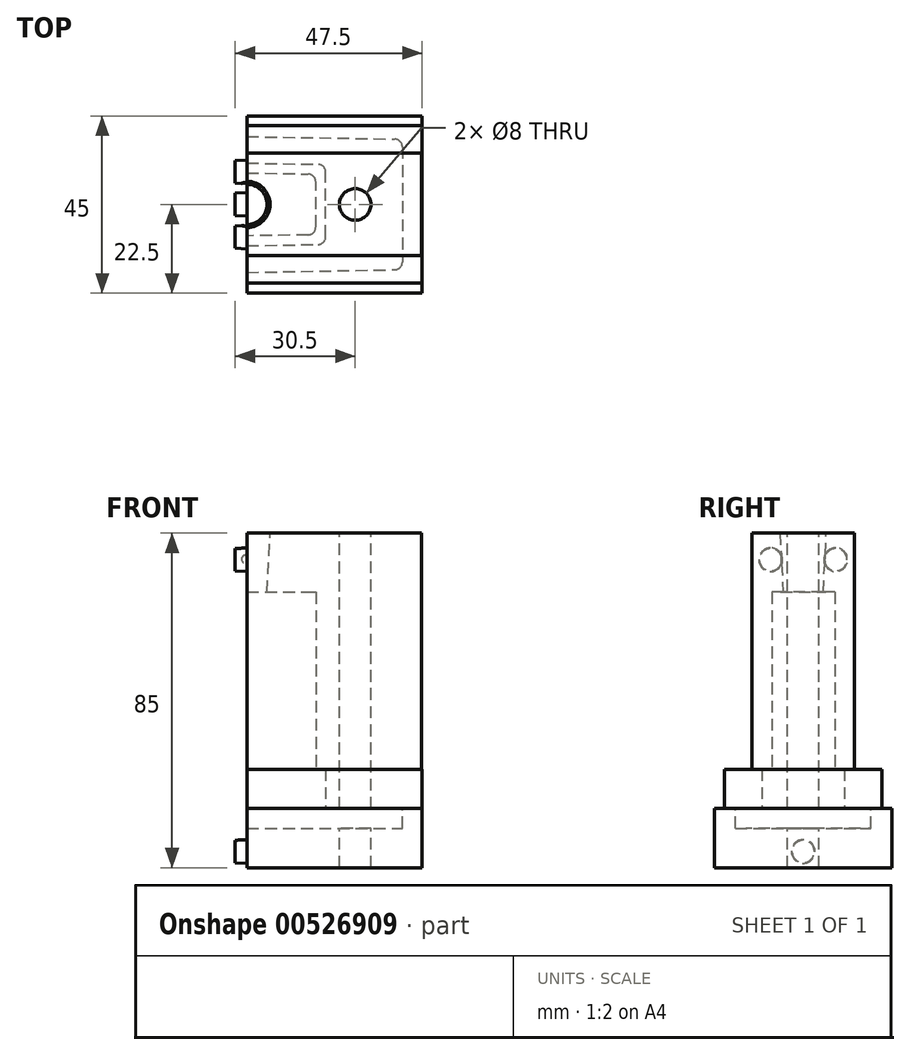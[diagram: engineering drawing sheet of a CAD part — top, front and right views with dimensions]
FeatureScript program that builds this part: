
annotation { "Feature Type Name" : "Feature", "Feature Type Description" : "" }
export const myFeature = defineFeature(function(context is Context, id is Id, definition is map)
    precondition{}
    {
        {
            var Q0;
            Q0=qCreatedBy(makeId("Top.planeOp"),FACE);
            var sketch = newSketch(context, id + "F0", { "sketchPlane" : qUnion([Q0])});
            skLineSegment(sketch, "E0.bottom", {"start": v(44.4, -13) * mm, "end": v(-44.4, -13) * mm});
            skLineSegment(sketch, "E0.top", {"start": v(44.4, 13) * mm, "end": v(-44.4, 13) * mm});
            skLineSegment(sketch, "E0.left", {"start": v(44.4, -13) * mm, "end": v(44.4, 13) * mm});
            skLineSegment(sketch, "E0.right", {"start": v(-44.4, -13) * mm, "end": v(-44.4, 13) * mm});
            skPoint(sketch, "E0.middle", {"position": v(0, 0) * mm});
            skSolve(sketch);
        }
        {
            var Q0;
            Q0 = qSketchRegion(id + "F0", true);
            extrude(context, id + "F1", {"entities" : qUnion([Q0]), "depth" : 60 * mm, "offsetDistance" : 25 * mm});
        }
        {
            var Q0;
            Q0=makeQuery(id+"F1.opExtrude","CAP_FACE",FACE,{"disambiguationData":[OSD([sQuery(id+"F0.wireOp",EDGE,"E0.bottom"),sQuery(id+"F0.wireOp",EDGE,"E0.top"),sQuery(id+"F0.wireOp",EDGE,"E0.left"),sQuery(id+"F0.wireOp",EDGE,"E0.right")])],"isStart":true});
            var sketch = newSketch(context, id + "F2", { "sketchPlane" : qUnion([Q0])});
            skPoint(sketch, "E1.middle", {"position": v(0, 0) * mm});
            skLineSegment(sketch, "E2", {"start": v(0, -8) * mm, "end": v(-17.5, -7.7) * mm});
            skLineSegment(sketch, "E3", {"start": v(0, -8) * mm, "end": v(17.5, -7.7) * mm});
            skLineSegment(sketch, "E4", {"start": v(0, 8) * mm, "end": v(-17.5, 7.7) * mm});
            skLineSegment(sketch, "E5", {"start": v(17.5, 7.7) * mm, "end": v(0, 8) * mm});
            skLineSegment(sketch, "E6", {"start": v(-17.5, 7.7) * mm, "end": v(-17.5, -7.7) * mm});
            skLineSegment(sketch, "E7", {"start": v(17.5, 7.7) * mm, "end": v(17.5, -7.7) * mm});
            skSolve(sketch);
        }
        {
            var Q0;
            Q0 = qSketchRegion(id + "F2", true);
            extrude(context, id + "F3", {"entities" : qUnion([Q0]), "operationType" : NewBodyOperationType.REMOVE, "oppositeDirection" : true, "depth" : 45 * mm, "offsetDistance" : 25 * mm});
        }
        {
            var Q0;
            Q0=makeQuery(id+"F3.boolean.opBoolean","COPY",EDGE,{"derivedFrom":makeQuery(id+"F3.opExtrude","SWEPT_EDGE",EDGE,{"disambiguationData":[OSD([sQuery(id+"F2.wireOp",EDGE,"E2"),sQuery(id+"F2.wireOp",EDGE,"E6")])]})});
            var Q1;
            Q1=makeQuery(id+"F3.boolean.opBoolean","COPY",EDGE,{"derivedFrom":makeQuery(id+"F3.opExtrude","SWEPT_EDGE",EDGE,{"disambiguationData":[OSD([sQuery(id+"F2.wireOp",EDGE,"E4"),sQuery(id+"F2.wireOp",EDGE,"E6")])]})});
            var Q2;
            Q2=makeQuery(id+"F3.boolean.opBoolean","COPY",EDGE,{"derivedFrom":makeQuery(id+"F3.opExtrude","SWEPT_EDGE",EDGE,{"disambiguationData":[OSD([sQuery(id+"F2.wireOp",EDGE,"E5"),sQuery(id+"F2.wireOp",EDGE,"E7")])]})});
            var Q3;
            Q3=makeQuery(id+"F3.boolean.opBoolean","COPY",EDGE,{"derivedFrom":makeQuery(id+"F3.opExtrude","SWEPT_EDGE",EDGE,{"disambiguationData":[OSD([sQuery(id+"F2.wireOp",EDGE,"E3"),sQuery(id+"F2.wireOp",EDGE,"E7")])]})});
            fillet(context, id + "F4", {"entities" : qUnion([Q0, Q1, Q2, Q3]), "radius" : 2 * mm, "tangentPropagation" : true, "allowEdgeOverflow" : false});
        }
        {
            var Q0;
            Q0=makeQuery(id+"F1.opExtrude","CAP_FACE",FACE,{"disambiguationData":[OSD([sQuery(id+"F0.wireOp",EDGE,"E0.bottom"),sQuery(id+"F0.wireOp",EDGE,"E0.top"),sQuery(id+"F0.wireOp",EDGE,"E0.left"),sQuery(id+"F0.wireOp",EDGE,"E0.right")])],"isStart":true});
            var sketch = newSketch(context, id + "F5", { "sketchPlane" : qUnion([Q0])});
            skLineSegment(sketch, "E8.bottom", {"start": v(44.45, -20) * mm, "end": v(-44.45, -20) * mm});
            skLineSegment(sketch, "E8.top", {"start": v(44.45, 20) * mm, "end": v(-44.45, 20) * mm});
            skLineSegment(sketch, "E8.left", {"start": v(44.45, -20) * mm, "end": v(44.45, 20) * mm});
            skLineSegment(sketch, "E8.right", {"start": v(-44.45, -20) * mm, "end": v(-44.45, 20) * mm});
            skPoint(sketch, "E8.middle", {"position": v(0, 0) * mm});
            skSolve(sketch);
        }
        {
            var Q0;
            Q0 = qSketchRegion(id + "F5", true);
            extrude(context, id + "F6", {"entities" : qUnion([Q0]), "operationType" : NewBodyOperationType.ADD, "depth" : 10 * mm, "offsetDistance" : 25 * mm});
        }
        {
            var Q0;
            Q0=makeQuery(id+"F6.opExtrude","CAP_FACE",FACE,{"disambiguationData":[OSD([sQuery(id+"F5.wireOp",EDGE,"E8.bottom"),sQuery(id+"F5.wireOp",EDGE,"E8.top"),sQuery(id+"F5.wireOp",EDGE,"E8.left"),sQuery(id+"F5.wireOp",EDGE,"E8.right")])],"isStart":false});
            var sketch = newSketch(context, id + "F7", { "sketchPlane" : qUnion([Q0])});
            skPoint(sketch, "E9.middle", {"position": v(0, 0) * mm});
            skLineSegment(sketch, "E10", {"start": v(0, -10.5) * mm, "end": v(20, -10.15) * mm});
            skLineSegment(sketch, "E11", {"start": v(0, -10.5) * mm, "end": v(-20, -10.15) * mm});
            skLineSegment(sketch, "E12", {"start": v(-20, 10.15) * mm, "end": v(0, 10.5) * mm});
            skLineSegment(sketch, "E13", {"start": v(0, 10.5) * mm, "end": v(20, 10.15) * mm});
            skLineSegment(sketch, "E14", {"start": v(20, 10.15) * mm, "end": v(20, -10.15) * mm});
            skLineSegment(sketch, "E15", {"start": v(-20, 10.15) * mm, "end": v(-20, -10.15) * mm});
            skSolve(sketch);
        }
        {
            var Q0;
            Q0 = qSketchRegion(id + "F7", true);
            extrude(context, id + "F8", {"entities" : qUnion([Q0]), "operationType" : NewBodyOperationType.REMOVE, "oppositeDirection" : true, "depth" : 10 * mm, "offsetDistance" : 25 * mm});
        }
        {
            var Q0;
            Q0=makeQuery(id+"F8.boolean.opBoolean","COPY",EDGE,{"derivedFrom":makeQuery(id+"F8.opExtrude","SWEPT_EDGE",EDGE,{"disambiguationData":[OSD([sQuery(id+"F7.wireOp",EDGE,"E11"),sQuery(id+"F7.wireOp",EDGE,"E15")])]})});
            var Q1;
            Q1=makeQuery(id+"F8.boolean.opBoolean","COPY",EDGE,{"derivedFrom":makeQuery(id+"F8.opExtrude","SWEPT_EDGE",EDGE,{"disambiguationData":[OSD([sQuery(id+"F7.wireOp",EDGE,"E12"),sQuery(id+"F7.wireOp",EDGE,"E15")])]})});
            var Q2;
            Q2=makeQuery(id+"F8.boolean.opBoolean","COPY",EDGE,{"derivedFrom":makeQuery(id+"F8.opExtrude","SWEPT_EDGE",EDGE,{"disambiguationData":[OSD([sQuery(id+"F7.wireOp",EDGE,"E10"),sQuery(id+"F7.wireOp",EDGE,"E14")])]})});
            var Q3;
            Q3=makeQuery(id+"F8.boolean.opBoolean","COPY",EDGE,{"derivedFrom":makeQuery(id+"F8.opExtrude","SWEPT_EDGE",EDGE,{"disambiguationData":[OSD([sQuery(id+"F7.wireOp",EDGE,"E13"),sQuery(id+"F7.wireOp",EDGE,"E14")])]})});
            fillet(context, id + "F9", {"entities" : qUnion([Q0, Q1, Q2, Q3]), "radius" : 2 * mm, "tangentPropagation" : true, "allowEdgeOverflow" : false});
        }
        {
            var Q0;
            Q0=makeQuery(id+"F6.opExtrude","CAP_FACE",FACE,{"disambiguationData":[OSD([sQuery(id+"F5.wireOp",EDGE,"E8.bottom"),sQuery(id+"F5.wireOp",EDGE,"E8.top"),sQuery(id+"F5.wireOp",EDGE,"E8.left"),sQuery(id+"F5.wireOp",EDGE,"E8.right")])],"isStart":false});
            var sketch = newSketch(context, id + "F10", { "sketchPlane" : qUnion([Q0])});
            skLineSegment(sketch, "E16.bottom", {"start": v(44.5, -22.5) * mm, "end": v(-44.5, -22.5) * mm});
            skLineSegment(sketch, "E16.top", {"start": v(44.5, 22.5) * mm, "end": v(-44.5, 22.5) * mm});
            skLineSegment(sketch, "E16.left", {"start": v(44.5, -22.5) * mm, "end": v(44.5, 22.5) * mm});
            skLineSegment(sketch, "E16.right", {"start": v(-44.5, -22.5) * mm, "end": v(-44.5, 22.5) * mm});
            skPoint(sketch, "E16.middle", {"position": v(0, 0) * mm});
            skSolve(sketch);
        }
        {
            var Q0;
            Q0 = qSketchRegion(id + "F10", true);
            extrude(context, id + "F11", {"entities" : qUnion([Q0]), "operationType" : NewBodyOperationType.ADD, "depth" : 15 * mm, "offsetDistance" : 25 * mm});
        }
        {
            var Q0;
            {var subQ0=sQuery(id+"F10.wireOp",EDGE,"E16.bottom");var subQ1=sQuery(id+"F10.wireOp",EDGE,"E16.top");var subQ2=sQuery(id+"F10.wireOp",EDGE,"E16.left");var subQ3=sQuery(id+"F10.wireOp",EDGE,"E16.right");Q0=makeQuery(id+"F11.boolean.opBoolean","SPLIT",FACE,{"disambiguationData":[TD([makeQuery(id+"F6.opExtrude","SWEPT_FACE",FACE,{"disambiguationData":[OSD([sQuery(id+"F5.wireOp",EDGE,"E8.bottom")])]})])],"derivedFrom":makeQuery(id+"F11.opExtrude","CAP_FACE",FACE,{"disambiguationData":[OSD([subQ0,subQ1,subQ2,subQ3])],"isStart":true})});}
            var sketch = newSketch(context, id + "F12", { "sketchPlane" : qUnion([Q0])});
            skPoint(sketch, "E17.middle", {"position": v(0, 0) * mm});
            skLineSegment(sketch, "E18", {"start": v(0, -17.25) * mm, "end": v(39.5, -16.56) * mm});
            skLineSegment(sketch, "E19", {"start": v(0, -17.25) * mm, "end": v(-44.45, -17.25) * mm});
            skLineSegment(sketch, "E20", {"start": v(-39.5, -16.56) * mm, "end": v(0, -17.25) * mm});
            skLineSegment(sketch, "E21", {"start": v(0, 17.25) * mm, "end": v(-39.5, 16.56) * mm});
            skLineSegment(sketch, "E22", {"start": v(0, 17.25) * mm, "end": v(39.5, 16.56) * mm});
            skLineSegment(sketch, "E23", {"start": v(-39.5, 16.56) * mm, "end": v(-39.5, -16.56) * mm});
            skLineSegment(sketch, "E24", {"start": v(39.5, 16.56) * mm, "end": v(39.5, -16.56) * mm});
            skSolve(sketch);
        }
        {
            var Q0;
            Q0 = qSketchRegion(id + "F12", true);
            extrude(context, id + "F13", {"entities" : qUnion([Q0]), "operationType" : NewBodyOperationType.REMOVE, "oppositeDirection" : true, "depth" : 5 * mm, "offsetDistance" : 25 * mm});
        }
        {
            var Q0;
            Q0=makeQuery(id+"F13.boolean.opBoolean","COPY",EDGE,{"derivedFrom":makeQuery(id+"F13.opExtrude","SWEPT_EDGE",EDGE,{"disambiguationData":[OSD([sQuery(id+"F12.wireOp",EDGE,"E21"),sQuery(id+"F12.wireOp",EDGE,"E23")])]})});
            var Q1;
            Q1=makeQuery(id+"F13.boolean.opBoolean","COPY",EDGE,{"derivedFrom":makeQuery(id+"F13.opExtrude","SWEPT_EDGE",EDGE,{"disambiguationData":[OSD([sQuery(id+"F12.wireOp",EDGE,"E20"),sQuery(id+"F12.wireOp",EDGE,"E23")])]})});
            var Q2;
            Q2=makeQuery(id+"F13.boolean.opBoolean","COPY",EDGE,{"derivedFrom":makeQuery(id+"F13.opExtrude","SWEPT_EDGE",EDGE,{"disambiguationData":[OSD([sQuery(id+"F12.wireOp",EDGE,"E18"),sQuery(id+"F12.wireOp",EDGE,"E24")])]})});
            var Q3;
            Q3=makeQuery(id+"F13.boolean.opBoolean","COPY",EDGE,{"derivedFrom":makeQuery(id+"F13.opExtrude","SWEPT_EDGE",EDGE,{"disambiguationData":[OSD([sQuery(id+"F12.wireOp",EDGE,"E22"),sQuery(id+"F12.wireOp",EDGE,"E24")])]})});
            fillet(context, id + "F14", {"entities" : qUnion([Q0, Q1, Q2, Q3]), "radius" : 2 * mm, "tangentPropagation" : true, "allowEdgeOverflow" : false});
        }
        {
            var Q0;
            Q0=makeQuery(id+"F1.opExtrude","CAP_FACE",FACE,{"disambiguationData":[OSD([sQuery(id+"F0.wireOp",EDGE,"E0.bottom"),sQuery(id+"F0.wireOp",EDGE,"E0.top"),sQuery(id+"F0.wireOp",EDGE,"E0.left"),sQuery(id+"F0.wireOp",EDGE,"E0.right")])],"isStart":false});
            var sketch = newSketch(context, id + "F15", { "sketchPlane" : qUnion([Q0])});
            skCircle(sketch, "E25", {"center": v(27.5, 0) * mm, "radius": 4 * mm});
            skCircle(sketch, "E26", {"center": v(-27.5, 0) * mm, "radius": 4.67 * mm});
            skSolve(sketch);
        }
        {
            var Q0;
            Q0=makeQuery(id+"F15.imprint","IMPRINT",FACE,{"disambiguationData":[TD([[makeQuery(id+"F15.imprint","IMPRINT",EDGE,{"derivedFrom":sQuery(id+"F15.wireOp",EDGE,"E26")}),1.0]])]});
            var Q1;
            Q1=makeQuery(id+"F15.imprint","IMPRINT",FACE,{"disambiguationData":[TD([[makeQuery(id+"F15.imprint","IMPRINT",EDGE,{"derivedFrom":sQuery(id+"F15.wireOp",EDGE,"E25")}),1.0]])]});
            var Q2;
            Q2=sQuery(id+"F15.wireOp",EDGE,"E26");
            var Q3;
            Q3=sQuery(id+"F15.wireOp",EDGE,"E25");
            extrude(context, id + "F16", {"entities" : qUnion([Q0, Q1]), "operationType" : NewBodyOperationType.REMOVE, "surfaceEntities" : qUnion([Q2, Q3]), "endBound" : BoundingType.THROUGH_ALL, "oppositeDirection" : true, "depth" : 90 * mm, "offsetDistance" : 25 * mm});
        }
        {
            var Q0;
            Q0=qCreatedBy(makeId("Right.planeOp"),FACE);
            var sketch = newSketch(context, id + "F17", { "sketchPlane" : qUnion([Q0])});
            skLineSegment(sketch, "E27.bottom", {"start": v(-35.8, 69.27) * mm, "end": v(43.73, 69.27) * mm});
            skLineSegment(sketch, "E27.top", {"start": v(-35.8, -49.53) * mm, "end": v(43.73, -49.53) * mm});
            skLineSegment(sketch, "E27.left", {"start": v(-35.8, 69.27) * mm, "end": v(-35.8, -49.53) * mm});
            skLineSegment(sketch, "E27.right", {"start": v(43.73, 69.27) * mm, "end": v(43.73, -49.53) * mm});
            skSolve(sketch);
        }
        {
            var Q0;
            Q0 = qSketchRegion(id + "F17", true);
            extrude(context, id + "F18", {"entities" : qUnion([Q0]), "operationType" : NewBodyOperationType.REMOVE, "oppositeDirection" : true, "depth" : 80 * mm, "offsetDistance" : 25 * mm});
        }
        {
            var Q0;
            Q0=makeQuery(id+"F18.boolean.opBoolean","COPY",FACE,{"derivedFrom":makeQuery(id+"F18.opExtrude","CAP_FACE",FACE,{"disambiguationData":[OSD([sQuery(id+"F17.wireOp",EDGE,"E27.bottom"),sQuery(id+"F17.wireOp",EDGE,"E27.top"),sQuery(id+"F17.wireOp",EDGE,"E27.left"),sQuery(id+"F17.wireOp",EDGE,"E27.right")])],"isStart":true})});
            var sketch = newSketch(context, id + "F19", { "sketchPlane" : qUnion([Q0])});
            skCircle(sketch, "E28", {"center": v(8.28, 53.23) * mm, "radius": 3 * mm});
            skCircle(sketch, "E29", {"center": v(0, -20.9) * mm, "radius": 3 * mm});
            skLineSegment(sketch, "E30", {"start": v(0, 60) * mm, "end": v(0, 81.48) * mm});
            skPoint(sketch, "E30.endSnap0", {"position": v(0, 60) * mm});
            skCircle(sketch, "E31.MirrorC", {"center": v(-8.28, 53.23) * mm, "radius": 3 * mm});
            skSolve(sketch);
        }
        {
            var Q0;
            Q0 = qSketchRegion(id + "F19", true);
            extrude(context, id + "F20", {"entities" : qUnion([Q0]), "operationType" : NewBodyOperationType.ADD, "depth" : 3 * mm, "offsetDistance" : 25 * mm, "hasDraft" : true, "draftAngle" : 3 * degree, "draftPullDirection" : true});
        }
        {
            var Q0;
            Q0 = qSketchRegion(id + "F19", true);
            extrude(context, id + "F21", {"entities" : qUnion([Q0]), "operationType" : NewBodyOperationType.ADD, "depth" : 3 * mm, "offsetDistance" : 25 * mm, "hasDraft" : true, "draftAngle" : 3 * degree, "draftPullDirection" : true});
        }
        {
            var Q0;
            Q0=makeQuery(id+"F3.boolean.opBoolean","COPY",FACE,{"derivedFrom":makeQuery(id+"F3.opExtrude","CAP_FACE",FACE,{"disambiguationData":[OSD([sQuery(id+"F2.wireOp",EDGE,"E2"),sQuery(id+"F2.wireOp",EDGE,"E3"),sQuery(id+"F2.wireOp",EDGE,"E4"),sQuery(id+"F2.wireOp",EDGE,"E5"),sQuery(id+"F2.wireOp",EDGE,"E6"),sQuery(id+"F2.wireOp",EDGE,"E7")])],"isStart":false})});
            var sketch = newSketch(context, id + "F22", { "sketchPlane" : qUnion([Q0])});
            skCircle(sketch, "E32", {"center": v(0, 0) * mm, "radius": 5.09 * mm});
            skSolve(sketch);
        }
        {
            var Q0;
            Q0 = qSketchRegion(id + "F22", true);
            extrude(context, id + "F23", {"entities" : qUnion([Q0]), "operationType" : NewBodyOperationType.REMOVE, "oppositeDirection" : true, "depth" : 25 * mm, "offsetDistance" : 25 * mm, "hasDraft" : true, "draftAngle" : 3 * degree});
        }
    });
